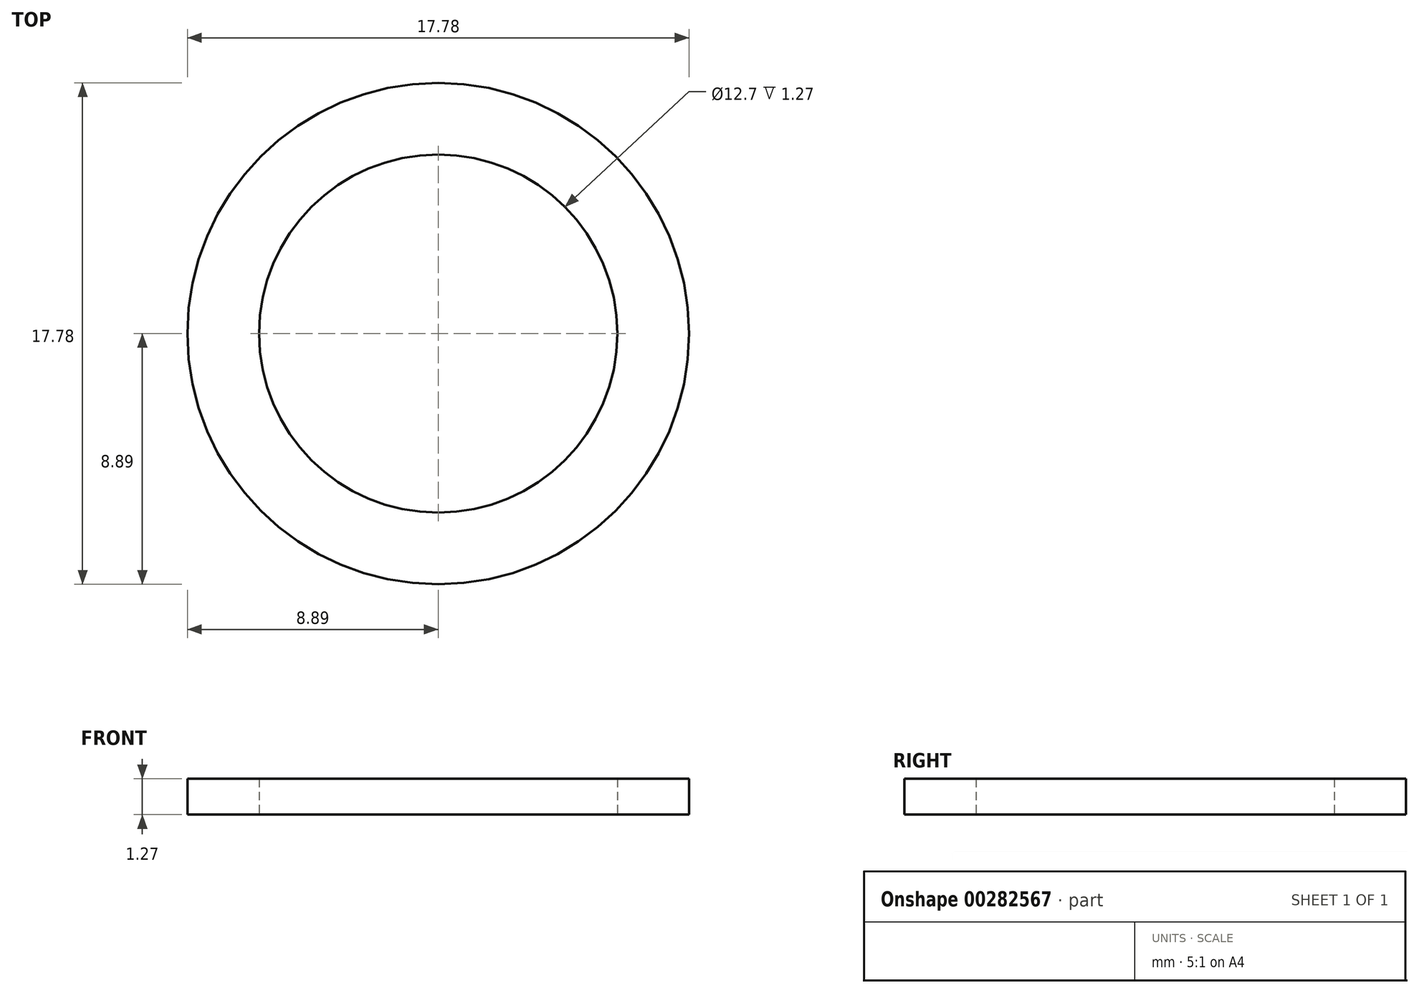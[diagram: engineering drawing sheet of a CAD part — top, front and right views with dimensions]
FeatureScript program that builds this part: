
annotation { "Feature Type Name" : "Feature", "Feature Type Description" : "" }
export const myFeature = defineFeature(function(context is Context, id is Id, definition is map)
    precondition{}
    {
        {
            var Q0;
            Q0=qCreatedBy(makeId("Top.planeOp"),FACE);
            var sketch = newSketch(context, id + "F0", { "sketchPlane" : qUnion([Q0])});
            skCircle(sketch, "E0", {"center": v(0, 0) * mm, "radius": 6.35 * mm});
            skCircle(sketch, "E1.0", {"center": v(0, 0) * mm, "radius": 8.9 * mm});
            skSolve(sketch);
        }
        {
            var Q0;
            Q0 = qSketchRegion(id + "F0", true);
            extrude(context, id + "F1", {"entities" : qUnion([Q0]), "depth" : 1.27 * mm});
        }
    });
